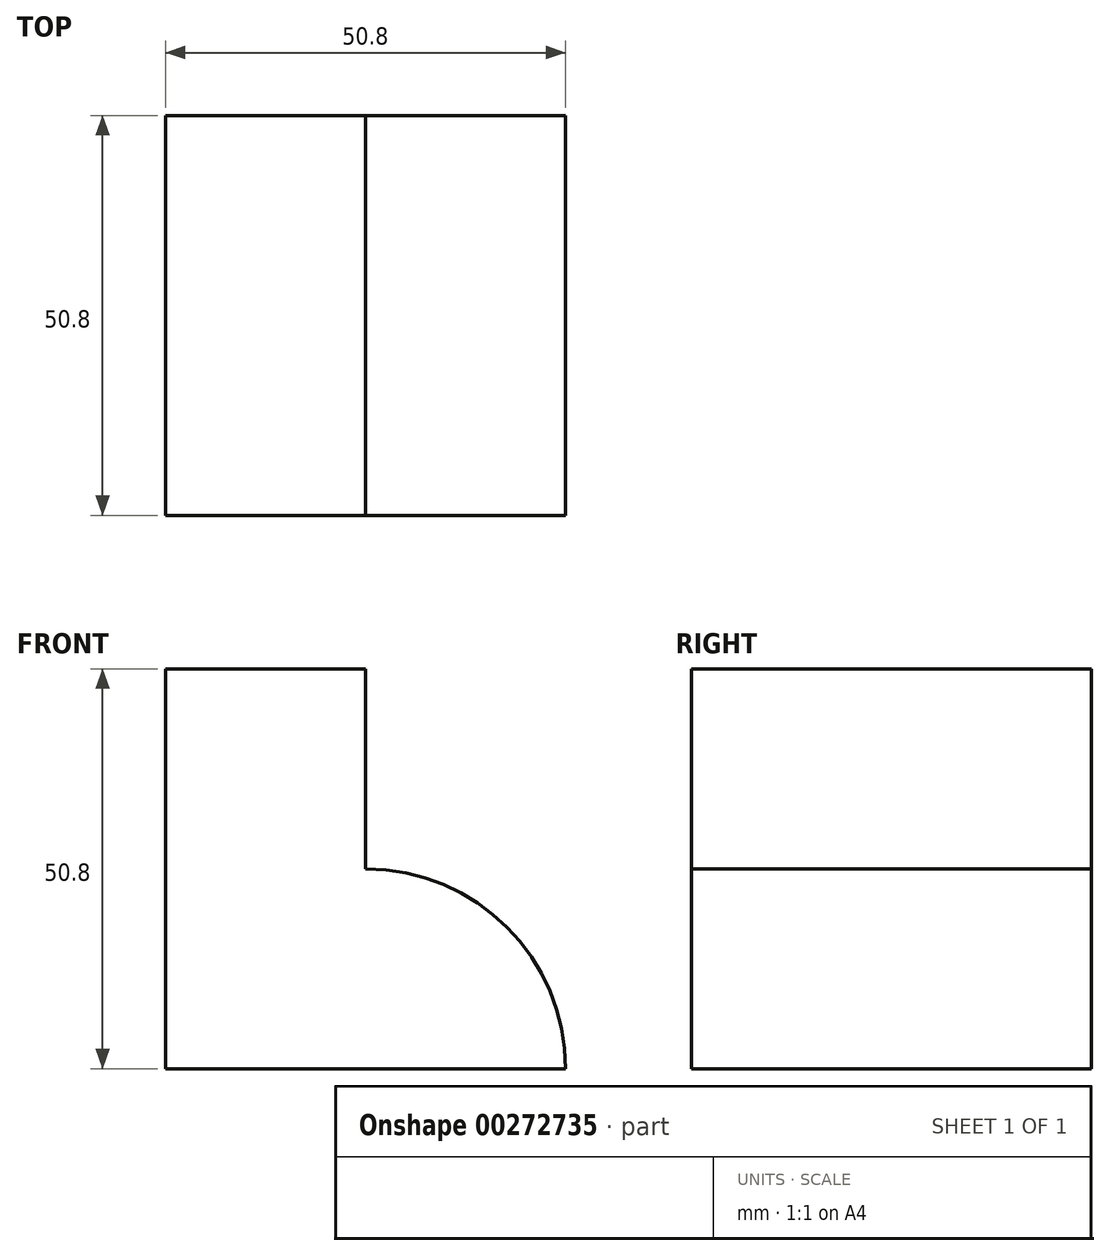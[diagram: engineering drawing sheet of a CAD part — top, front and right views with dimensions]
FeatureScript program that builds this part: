
annotation { "Feature Type Name" : "Feature", "Feature Type Description" : "" }
export const myFeature = defineFeature(function(context is Context, id is Id, definition is map)
    precondition{}
    {
        {
            var Q0;
            Q0=qCreatedBy(makeId("Front.planeOp"),FACE);
            var sketch = newSketch(context, id + "F0", { "sketchPlane" : qUnion([Q0])});
            skLineSegment(sketch, "E0", {"start": v(0, 0) * mm, "end": v(-50.8, 0) * mm});
            skLineSegment(sketch, "E1", {"start": v(-50.8, 0) * mm, "end": v(-50.8, 50.8) * mm});
            skLineSegment(sketch, "E2", {"start": v(-50.8, 50.8) * mm, "end": v(-25.4, 50.8) * mm});
            skLineSegment(sketch, "E3", {"start": v(-25.4, 50.8) * mm, "end": v(-25.4, 25.4) * mm});
            skArc(sketch, "E4", {"start": v(0, 0) * mm, "mid": v(-7.44, 17.96) * mm, "end": v(-25.4, 25.4) * mm});
            skSolve(sketch);
        }
        {
            var Q0;
            Q0 = qSketchRegion(id + "F0", true);
            extrude(context, id + "F1", {"entities" : qUnion([Q0]), "depth" : 50.8 * mm});
        }
    });
